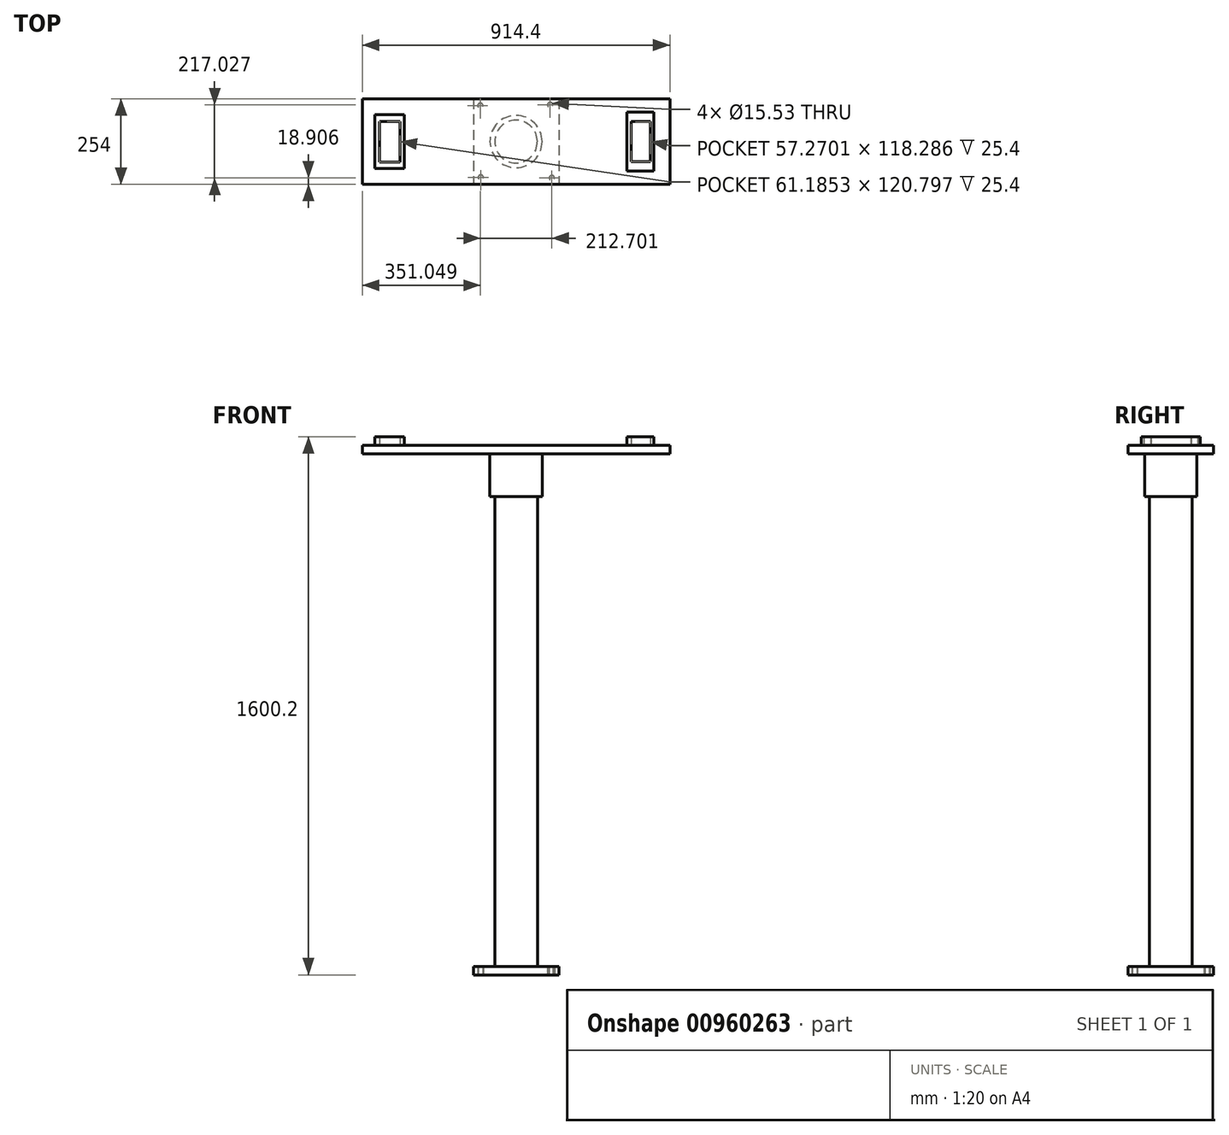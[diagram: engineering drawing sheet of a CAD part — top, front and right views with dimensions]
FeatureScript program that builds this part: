
annotation { "Feature Type Name" : "Feature", "Feature Type Description" : "" }
export const myFeature = defineFeature(function(context is Context, id is Id, definition is map)
    precondition{}
    {
        {
            var Q0;
            Q0=qCreatedBy(makeId("Top.planeOp"),FACE);
            var sketch = newSketch(context, id + "F0", { "sketchPlane" : qUnion([Q0])});
            skLineSegment(sketch, "E0.bottom", {"start": v(-127, 127) * mm, "end": v(127, 127) * mm});
            skLineSegment(sketch, "E0.top", {"start": v(-127, -127) * mm, "end": v(127, -127) * mm});
            skLineSegment(sketch, "E0.left", {"start": v(-127, 127) * mm, "end": v(-127, -127) * mm});
            skLineSegment(sketch, "E0.right", {"start": v(127, 127) * mm, "end": v(127, -127) * mm});
            skPoint(sketch, "E0.middle", {"position": v(0, 0) * mm});
            skCircle(sketch, "E1", {"center": v(0, 0) * mm, "radius": 62.45 * mm});
            skCircle(sketch, "E2", {"center": v(-106.15, 106.77) * mm, "radius": 7.77 * mm});
            skCircle(sketch, "E3", {"center": v(101.5, 108.93) * mm, "radius": 7.77 * mm});
            skCircle(sketch, "E4", {"center": v(106.55, -108.1) * mm, "radius": 7.77 * mm});
            skCircle(sketch, "E5", {"center": v(-104.7, -106.65) * mm, "radius": 7.77 * mm});
            skSolve(sketch);
        }
        {
            var Q0;
            Q0=makeQuery(id+"F0.imprint","IMPRINT",FACE,{"disambiguationData":[TD([[makeQuery(id+"F0.imprint","IMPRINT",EDGE,{"derivedFrom":sQuery(id+"F0.wireOp",EDGE,"E0.bottom")}),-1.0]])]});
            var Q1;
            Q1=makeQuery(id+"F0.imprint","IMPRINT",FACE,{"disambiguationData":[TD([[makeQuery(id+"F0.imprint","IMPRINT",EDGE,{"derivedFrom":sQuery(id+"F0.wireOp",EDGE,"E1")}),1.0]])]});
            extrude(context, id + "F1", {"entities" : qUnion([Q0, Q1]), "depth" : 25.4 * mm, "offsetDistance" : 25.4 * mm});
        }
        {
            var Q0;
            Q0=makeQuery(id+"F1.opExtrude","CAP_FACE",FACE,{"disambiguationData":[OSD([sQuery(id+"F0.wireOp",EDGE,"E0.bottom"),sQuery(id+"F0.wireOp",EDGE,"E0.top"),sQuery(id+"F0.wireOp",EDGE,"E0.left"),sQuery(id+"F0.wireOp",EDGE,"E0.right"),sQuery(id+"F0.wireOp",EDGE,"E2"),sQuery(id+"F0.wireOp",EDGE,"E3"),sQuery(id+"F0.wireOp",EDGE,"E4"),sQuery(id+"F0.wireOp",EDGE,"E5")])],"isStart":false});
            var sketch = newSketch(context, id + "F2", { "sketchPlane" : qUnion([Q0])});
            skCircle(sketch, "E6", {"center": v(0, 0) * mm, "radius": 63.5 * mm});
            skSolve(sketch);
        }
        {
            var Q0;
            Q0=makeQuery(id+"F2.imprint","IMPRINT",FACE,{"disambiguationData":[TD([[makeQuery(id+"F2.imprint","IMPRINT",EDGE,{"derivedFrom":sQuery(id+"F2.wireOp",EDGE,"E6")}),1.0]])]});
            extrude(context, id + "F3", {"entities" : qUnion([Q0]), "operationType" : NewBodyOperationType.ADD, "depth" : 1524 * mm, "offsetDistance" : 25.4 * mm});
        }
        {
            var Q0;
            Q0=makeQuery(id+"F3.opExtrude","CAP_FACE",FACE,{"disambiguationData":[OSD([sQuery(id+"F2.wireOp",EDGE,"E6")])],"isStart":false});
            var sketch = newSketch(context, id + "F4", { "sketchPlane" : qUnion([Q0])});
            skLineSegment(sketch, "E7.bottom", {"start": v(457.2, -127) * mm, "end": v(-457.2, -127) * mm});
            skLineSegment(sketch, "E7.top", {"start": v(457.2, 127) * mm, "end": v(-457.2, 127) * mm});
            skLineSegment(sketch, "E7.left", {"start": v(457.2, -127) * mm, "end": v(457.2, 127) * mm});
            skLineSegment(sketch, "E7.right", {"start": v(-457.2, -127) * mm, "end": v(-457.2, 127) * mm});
            skPoint(sketch, "E7.middle", {"position": v(0, 0) * mm});
            skSolve(sketch);
        }
        {
            var Q0;
            Q0=makeQuery(id+"F4.imprint","IMPRINT",FACE,{"disambiguationData":[TD([[makeQuery(id+"F4.imprint","IMPRINT",EDGE,{"derivedFrom":makeQuery(id+"F3.opExtrude","CAP_EDGE",EDGE,{"disambiguationData":[OSD([sQuery(id+"F2.wireOp",EDGE,"E6")])],"isStart":false})}),1.0]])]});
            extrude(context, id + "F5", {"entities" : qUnion([Q0]), "operationType" : NewBodyOperationType.ADD, "depth" : 25.4 * mm, "offsetDistance" : 25.4 * mm});
        }
        {
            var Q0;
            Q0=makeQuery(id+"F4.imprint","IMPRINT",FACE,{"disambiguationData":[TD([[makeQuery(id+"F4.imprint","IMPRINT",EDGE,{"derivedFrom":sQuery(id+"F4.wireOp",EDGE,"E7.bottom")}),-1.0]])]});
            extrude(context, id + "F6", {"entities" : qUnion([Q0]), "operationType" : NewBodyOperationType.ADD, "depth" : 25.4 * mm, "offsetDistance" : 25.4 * mm});
        }
        {
            var Q0;
            {var subQ0=sQuery(id+"F2.wireOp",EDGE,"E6");Q0=makeQuery(id+"F6.boolean.opBoolean","MERGE",FACE,{"derivedFrom":[makeQuery(id+"F5.opExtrude","CAP_FACE",FACE,{"disambiguationData":[OSD([subQ0])],"isStart":false}),makeQuery(id+"F6.opExtrude","CAP_FACE",FACE,{"disambiguationData":[OSD([subQ0,sQuery(id+"F4.wireOp",EDGE,"E7.bottom"),sQuery(id+"F4.wireOp",EDGE,"E7.top"),sQuery(id+"F4.wireOp",EDGE,"E7.left"),sQuery(id+"F4.wireOp",EDGE,"E7.right")])],"isStart":false})]});}
            var sketch = newSketch(context, id + "F7", { "sketchPlane" : qUnion([Q0])});
            skLineSegment(sketch, "E8.bottom", {"start": v(329.96, 87.62) * mm, "end": v(409.8, 87.62) * mm});
            skLineSegment(sketch, "E8.top", {"start": v(329.96, -87.62) * mm, "end": v(409.8, -87.62) * mm});
            skLineSegment(sketch, "E8.left", {"start": v(329.96, 87.62) * mm, "end": v(329.96, -87.62) * mm});
            skLineSegment(sketch, "E8.right", {"start": v(409.8, 87.62) * mm, "end": v(409.8, -87.62) * mm});
            skPoint(sketch, "E8.middle", {"position": v(369.88, 0) * mm});
            skSolve(sketch);
        }
        {
            var Q0;
            Q0=makeQuery(id+"F7.imprint","IMPRINT",FACE,{"disambiguationData":[TD([[makeQuery(id+"F7.imprint","IMPRINT",EDGE,{"derivedFrom":sQuery(id+"F7.wireOp",EDGE,"E8.bottom")}),-1.0]])]});
            var sketch = newSketch(context, id + "F8", { "sketchPlane" : qUnion([Q0])});
            skLineSegment(sketch, "E9.bottom", {"start": v(399.22, 59.14) * mm, "end": v(341.95, 59.14) * mm});
            skLineSegment(sketch, "E9.top", {"start": v(399.22, -59.14) * mm, "end": v(341.95, -59.14) * mm});
            skLineSegment(sketch, "E9.left", {"start": v(399.22, 59.14) * mm, "end": v(399.22, -59.14) * mm});
            skLineSegment(sketch, "E9.right", {"start": v(341.95, 59.14) * mm, "end": v(341.95, -59.14) * mm});
            skPoint(sketch, "E9.middle", {"position": v(370.58, 0) * mm});
            skSolve(sketch);
        }
        {
            var Q0;
            Q0=makeQuery(id+"F8.imprint","IMPRINT",FACE,{"disambiguationData":[TD([[makeQuery(id+"F8.imprint","IMPRINT",EDGE,{"derivedFrom":sQuery(id+"F8.wireOp",EDGE,"E9.bottom")}),-1.0]])]});
            var sketch = newSketch(context, id + "F9", { "sketchPlane" : qUnion([Q0])});
            skLineSegment(sketch, "E10.bottom", {"start": v(349.09, 68.6) * mm, "end": v(394.63, 68.6) * mm});
            skLineSegment(sketch, "E10.top", {"start": v(349.09, 79.16) * mm, "end": v(394.63, 79.16) * mm});
            skLineSegment(sketch, "E10.left", {"start": v(349.09, 68.6) * mm, "end": v(349.09, 79.16) * mm});
            skLineSegment(sketch, "E10.right", {"start": v(394.63, 68.6) * mm, "end": v(394.63, 79.16) * mm});
            skPoint(sketch, "E10.middle", {"position": v(371.86, 73.88) * mm});
            skSolve(sketch);
        }
        {
            var Q0;
            Q0=makeQuery(id+"F8.imprint","IMPRINT",FACE,{"disambiguationData":[TD([[makeQuery(id+"F8.imprint","IMPRINT",EDGE,{"derivedFrom":sQuery(id+"F8.wireOp",EDGE,"E9.bottom")}),-1.0]])]});
            var Q1;
            Q1=makeQuery(id+"F9.imprint","IMPRINT",FACE,{"disambiguationData":[TD([[makeQuery(id+"F9.imprint","IMPRINT",EDGE,{"derivedFrom":sQuery(id+"F9.wireOp",EDGE,"E10.bottom")}),-1.0]])]});
            extrude(context, id + "F10", {"entities" : qUnion([Q0, Q1]), "operationType" : NewBodyOperationType.ADD, "depth" : 25.4 * mm, "offsetDistance" : 25.4 * mm});
        }
        {
            var Q0;
            Q0=makeQuery(id+"F7.imprint","IMPRINT",FACE,{"disambiguationData":[TD([[makeQuery(id+"F7.imprint","IMPRINT",EDGE,{"derivedFrom":sQuery(id+"F7.wireOp",EDGE,"E8.bottom")}),1.0]])]});
            var sketch = newSketch(context, id + "F11", { "sketchPlane" : qUnion([Q0])});
            skLineSegment(sketch, "E11.bottom", {"start": v(-419.19, 79.85) * mm, "end": v(-332.34, 79.85) * mm});
            skLineSegment(sketch, "E11.top", {"start": v(-419.19, -79.85) * mm, "end": v(-332.34, -79.85) * mm});
            skLineSegment(sketch, "E11.left", {"start": v(-419.19, 79.85) * mm, "end": v(-419.19, -79.85) * mm});
            skLineSegment(sketch, "E11.right", {"start": v(-332.34, 79.85) * mm, "end": v(-332.34, -79.85) * mm});
            skPoint(sketch, "E11.middle", {"position": v(-375.77, 0) * mm});
            skLineSegment(sketch, "E12.bottom", {"start": v(-345.17, 60.4) * mm, "end": v(-406.36, 60.4) * mm});
            skLineSegment(sketch, "E12.top", {"start": v(-345.17, -60.4) * mm, "end": v(-406.36, -60.4) * mm});
            skLineSegment(sketch, "E12.left", {"start": v(-345.17, 60.4) * mm, "end": v(-345.17, -60.4) * mm});
            skLineSegment(sketch, "E12.right", {"start": v(-406.36, 60.4) * mm, "end": v(-406.36, -60.4) * mm});
            skSolve(sketch);
        }
        {
            var Q0;
            Q0=makeQuery(id+"F11.imprint","IMPRINT",FACE,{"disambiguationData":[TD([[makeQuery(id+"F11.imprint","IMPRINT",EDGE,{"derivedFrom":sQuery(id+"F11.wireOp",EDGE,"E11.bottom")}),-1.0]])]});
            extrude(context, id + "F12", {"entities" : qUnion([Q0]), "operationType" : NewBodyOperationType.ADD, "depth" : 25.4 * mm, "offsetDistance" : 25.4 * mm});
        }
        {
            var Q0;
            Q0=makeQuery(id+"F4.imprint","IMPRINT",FACE,{"disambiguationData":[TD([[makeQuery(id+"F4.imprint","IMPRINT",EDGE,{"derivedFrom":sQuery(id+"F4.wireOp",EDGE,"E7.bottom")}),-1.0]])]});
            var sketch = newSketch(context, id + "F13", { "sketchPlane" : qUnion([Q0])});
            skCircle(sketch, "E13", {"center": v(0, 0) * mm, "radius": 77.71 * mm});
            skSolve(sketch);
        }
        {
            var Q0;
            Q0 = qSketchRegion(id + "F13", true);
            extrude(context, id + "F14", {"entities" : qUnion([Q0]), "operationType" : NewBodyOperationType.ADD, "oppositeDirection" : true, "depth" : 127 * mm, "offsetDistance" : 25.4 * mm});
        }
    });
